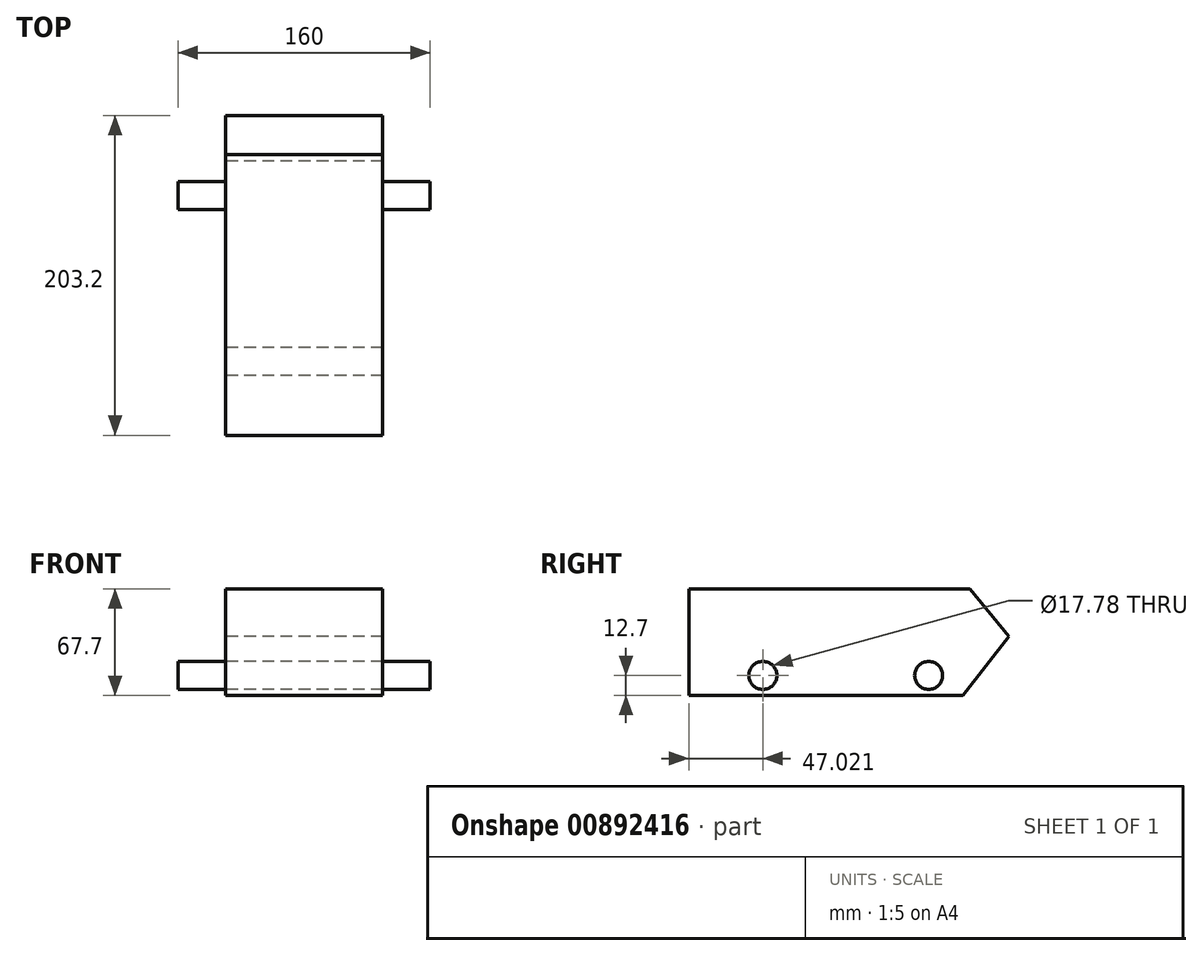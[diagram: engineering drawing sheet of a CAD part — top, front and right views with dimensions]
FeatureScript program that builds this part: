
annotation { "Feature Type Name" : "Feature", "Feature Type Description" : "" }
export const myFeature = defineFeature(function(context is Context, id is Id, definition is map)
    precondition{}
    {
        {
            var Q0;
            Q0=qCreatedBy(makeId("Right.planeOp"),FACE);
            var sketch = newSketch(context, id + "F0", { "sketchPlane" : qUnion([Q0])});
            skLineSegment(sketch, "E0.bottom", {"start": v(101.6, -50.8) * mm, "end": v(-101.6, -50.8) * mm});
            skLineSegment(sketch, "E0.top", {"start": v(101.6, 50.8) * mm, "end": v(-101.6, 50.8) * mm});
            skLineSegment(sketch, "E0.left", {"start": v(101.6, -50.8) * mm, "end": v(101.6, 50.8) * mm});
            skLineSegment(sketch, "E0.right", {"start": v(-101.6, -50.8) * mm, "end": v(-101.6, 50.8) * mm});
            skPoint(sketch, "E0.middle", {"position": v(0, 0) * mm});
            skCircle(sketch, "E1", {"center": v(-54.58, -38.1) * mm, "radius": 8.9 * mm});
            skCircle(sketch, "E2", {"center": v(50.7, -38.1) * mm, "radius": 8.9 * mm});
            skCircle(sketch, "E3", {"center": v(-169.3, -61.47) * mm, "radius": 54.61 * mm});
            skCircle(sketch, "E4", {"center": v(-216.35, 87.36) * mm, "radius": 54.61 * mm});
            skLineSegment(sketch, "E5", {"start": v(49.02, 50.8) * mm, "end": v(101.6, -13.32) * mm});
            skLineSegment(sketch, "E6", {"start": v(101.6, -13.32) * mm, "end": v(72.48, -50.8) * mm});
            skSolve(sketch);
        }
        {
            var Q0;
            {var subQ0=sQuery(id+"F0.wireOp",EDGE,"E0.right");Q0=makeQuery(id+"F0.imprint","IMPRINT",FACE,{"disambiguationData":[TD([[makeQuery(id+"F0.imprint","IMPRINT",EDGE,{"derivedFrom":subQ0}),-1.0]])]});}
            extrude(context, id + "F1", {"entities" : qUnion([Q0]), "depth" : 50 * mm, "offsetDistance" : 25.4 * mm});
        }
        {
            var Q0;
            Q0=makeQuery(id+"F1.opExtrude","CAP_FACE",FACE,{"disambiguationData":[OSD([sQuery(id+"F0.wireOp",EDGE,"E0.bottom"),sQuery(id+"F0.wireOp",EDGE,"E0.top"),sQuery(id+"F0.wireOp",EDGE,"E0.left"),sQuery(id+"F0.wireOp",EDGE,"E0.right"),sQuery(id+"F0.wireOp",EDGE,"E1"),sQuery(id+"F0.wireOp",EDGE,"E2"),sQuery(id+"F0.wireOp",EDGE,"E5")])],"isStart":false});
            var sketch = newSketch(context, id + "F2", { "sketchPlane" : qUnion([Q0])});
            skLineSegment(sketch, "E7", {"start": v(-101.6, 16.9) * mm, "end": v(76.82, 16.9) * mm});
            skSolve(sketch);
        }
        {
            var Q0;
            {var subQ0=sQuery(id+"F2.wireOp",EDGE,"E7");Q0=makeQuery(id+"F2.imprint","IMPRINT",FACE,{"disambiguationData":[TD([[makeQuery(id+"F2.imprint","IMPRINT",EDGE,{"derivedFrom":subQ0}),1.0]])]});}
            extrude(context, id + "F3", {"entities" : qUnion([Q0]), "operationType" : NewBodyOperationType.REMOVE, "oppositeDirection" : true, "depth" : 50 * mm, "offsetDistance" : 25 * mm});
        }
        {
            var Q0;
            Q0=makeQuery(id+"F0.imprint","IMPRINT",FACE,{"disambiguationData":[TD([[makeQuery(id+"F0.imprint","IMPRINT",EDGE,{"derivedFrom":sQuery(id+"F0.wireOp",EDGE,"E2")}),1.0]])]});
            extrude(context, id + "F4", {"entities" : qUnion([Q0]), "operationType" : NewBodyOperationType.ADD, "depth" : 80 * mm, "offsetDistance" : 25 * mm});
        }
        {
            var Q0;
            Q0=makeQuery(id+"F1.opExtrude","SWEPT_BODY",BODY,{"disambiguationData":[OSD([sQuery(id+"F0.wireOp",EDGE,"E0.bottom"),sQuery(id+"F0.wireOp",EDGE,"E0.top"),sQuery(id+"F0.wireOp",EDGE,"E0.right"),sQuery(id+"F0.wireOp",EDGE,"E1"),sQuery(id+"F0.wireOp",EDGE,"E2"),sQuery(id+"F0.wireOp",EDGE,"E5"),sQuery(id+"F0.wireOp",EDGE,"E6")])]});
            var Q1;
            Q1=qCreatedBy(makeId("Right.planeOp"),FACE);
            mirror(context, id + "F5", {"operationType" : NewBodyOperationType.ADD, "entities" : qUnion([Q0]), "mirrorPlane" : qUnion([Q1])});
        }
    });
